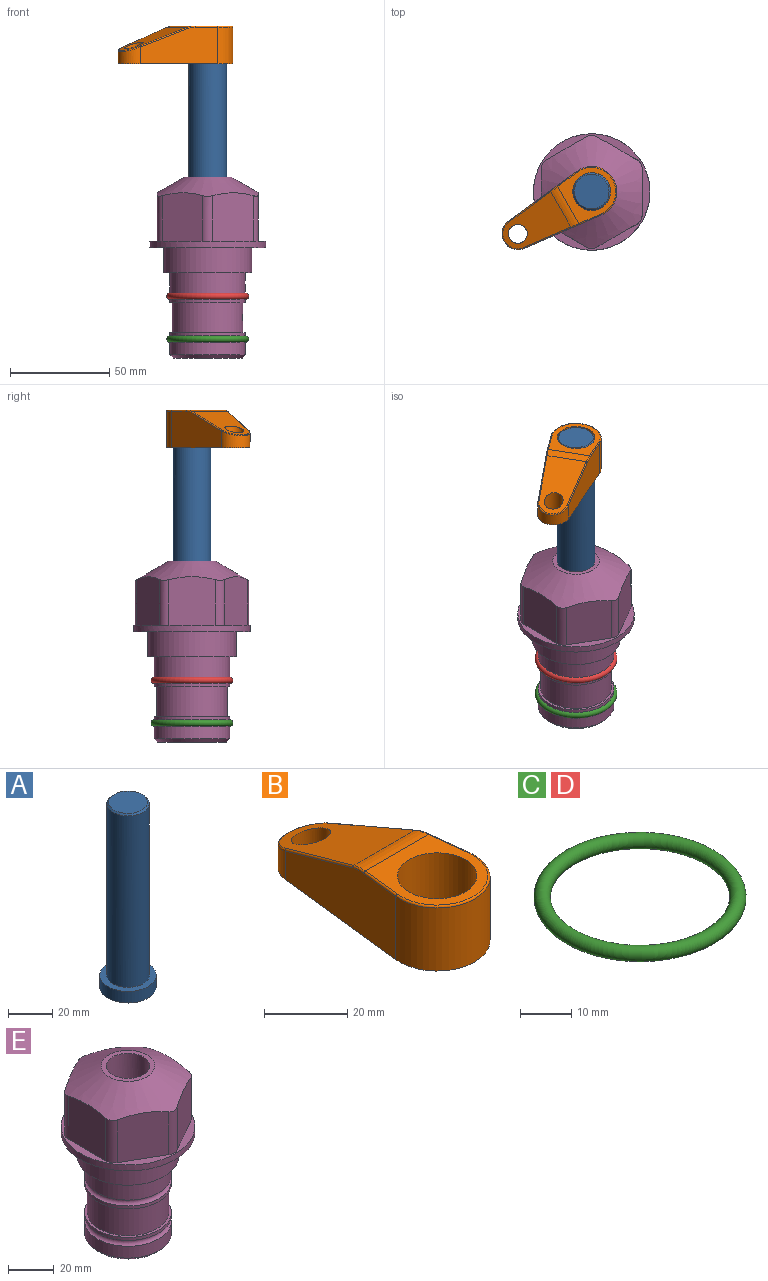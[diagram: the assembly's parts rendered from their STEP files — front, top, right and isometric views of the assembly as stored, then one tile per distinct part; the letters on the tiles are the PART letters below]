
ASSEMBLY  parts=5 mates=3
PART A: 6 faces, bbox 25.4x25.4x101.6 mm
  f0: plane 17.46x17.46mm, normal (0,0,1), area 239.5mm2, adj f5
  f1: plane 25.4x25.4mm, normal (0,0,-1), area 506.7mm2, adj f2
  f2: cylinder r=12.7mm len=25.4mm, axis (0,0,1), area 506.7mm2, adj f1,f3
  f3: plane 25.4x25.4mm, normal (0,0,1), area 221.7mm2, adj f2,f4
  f4: cylinder r=9.53mm len=94.46mm, axis (0,0,1), area 5653mm2, adj f3,f5
  f5: cone r=8.73mm half-angle=45deg, axis (0,0,-1), area 64.4mm2, adj f0,f4
PART B: 44 faces, bbox 27.5x64.5x19.1 mm
  f0: plane 2.3x0.95mm, normal (0,0,-1), area 1mm2, adj f25,f30,f34
  f1: plane 63.5x25.4mm, normal (0,0,-1), area 561.7mm2, adj f2,f3,f4,f5,f6,f7,f19,f20
  f2: cylinder r=12.7mm len=25.4mm, axis (0,0,-1), area 792.2mm2, adj f1,f3,f5,f13
  f3: plane 42.33x18.54mm, normal (0.99,0.11,0), area 647mm2, adj f1,f2,f4,f11,f12,f14
  f4: cylinder r=7.94mm len=15.78mm, axis (0,0,-1), area 158.6mm2, adj f1,f3,f5,f16
  f5: plane 42.33x18.54mm, normal (-0.99,0.11,0), area 647mm2, adj f1,f2,f4,f15,f17,f18
  f6: cylinder r=9.53mm len=19.05mm, axis (0,0,-1), area 1140.1mm2, adj f1,f8
  f7: cylinder r=4.76mm len=10.98mm, axis (0,0,-1), area 276.1mm2, adj f1,f9
  f8: plane 25.83x24.38mm, normal (0,0,1), area 262.2mm2, adj f6,f10,f11,f13,f15
  f9: plane 32.49x20.55mm, normal (0,0.34,0.94), area 489.9mm2, adj f7,f10,f14,f16,f18
  f10: cylinder r=12.7mm len=21.49mm, axis (-1,0,0), area 93.2mm2, adj f8,f9,f12,f17
  f11: cylinder r=0.51mm len=12.34mm, axis (0.11,-0.99,0), area 9.9mm2, adj f3,f8,f12,f13
  f12: bspline ~7.62x1.64mm, area 3.5mm2, adj f3,f10,f11,f14
  f13: torus R=12.19mm, axis (0,0,1), area 33.6mm2, adj f2,f8,f11,f15
  f14: cylinder r=0.51mm len=26.01mm, axis (0.1,-0.93,0.34), area 21.6mm2, adj f3,f9,f12,f16
  f15: cylinder r=0.51mm len=12.34mm, axis (0.11,0.99,0), area 9.9mm2, adj f5,f8,f13,f17
  f16: bspline ~15.78x7.05mm, area 15.7mm2, adj f4,f9,f14,f18
  f17: bspline ~7.62x1.64mm, area 3.5mm2, adj f5,f10,f15,f18
  f18: cylinder r=0.51mm len=26.01mm, axis (0.1,0.93,-0.34), area 21.6mm2, adj f5,f9,f16,f17
  f19: plane 21.6x14.29mm, normal (-0.99,-0.11,0), area 242.6mm2, adj f1,f26,f28,f34,f36,f38
  f20: plane 21.6x14.29mm, normal (0.99,-0.11,0), area 242.6mm2, adj f1,f27,f29,f37,f39,f41
  f21: cylinder r=12.7mm len=14.29mm, axis (0,0,-1), area 173.2mm2, adj f1,f26,f27,f30,f31,f33
  f22: cylinder r=7.94mm len=7.63mm, axis (0,0,-1), area 53.8mm2, adj f1,f28,f29,f42
  f23: plane 2.3x0.95mm, normal (0,0,-1), area 1mm2, adj f25,f33,f37
  f24: plane 17.94x12.32mm, normal (0,-0.34,-0.94), area 191.2mm2, adj f25,f38,f41,f42
  f25: cylinder r=9.53mm len=12.93mm, axis (-1,0,0), area 37.5mm2, adj f0,f23,f24,f31,f36,f39
  f26: cylinder r=1.59mm len=14.29mm, axis (0,0,-1), area 49mm2, adj f1,f19,f21,f32
  f27: cylinder r=1.59mm len=14.29mm, axis (0,0,-1), area 49mm2, adj f1,f20,f21,f35
  f28: cylinder r=1.59mm len=7.28mm, axis (0,0,-1), area 22.1mm2, adj f1,f19,f22,f40
  f29: cylinder r=1.59mm len=7.28mm, axis (0,0,-1), area 22.1mm2, adj f1,f20,f22,f43
  f30: torus R=14.29mm, axis (0,0,1), area 5.8mm2, adj f0,f21,f31,f32
  f31: bspline ~11.06x2.73mm, area 20.8mm2, adj f21,f25,f30,f33
  f32: sphere r=1.59mm, area 5.4mm2, adj f26,f30,f34
  f33: torus R=14.29mm, axis (0,0,1), area 5.8mm2, adj f21,f23,f31,f35
  f34: cylinder r=1.59mm len=1.68mm, axis (-0.11,0.99,0), area 2.4mm2, adj f0,f19,f32,f36
  f35: sphere r=1.59mm, area 5.4mm2, adj f27,f33,f37
  f36: bspline ~5.82x2.33mm, area 7.7mm2, adj f19,f25,f34,f38
  f37: cylinder r=1.59mm len=1.68mm, axis (0.11,0.99,0), area 2.4mm2, adj f20,f23,f35,f39
  f38: cylinder r=1.59mm len=18.33mm, axis (0.1,-0.93,0.34), area 46.7mm2, adj f19,f24,f36,f40
  f39: bspline ~5.82x2.33mm, area 7.7mm2, adj f20,f25,f37,f41
  f40: sphere r=1.59mm, area 3.6mm2, adj f28,f38,f42
  f41: cylinder r=1.59mm len=18.33mm, axis (0.1,0.93,-0.34), area 46.7mm2, adj f20,f24,f39,f43
  f42: bspline ~8.31x1.84mm, area 15.3mm2, adj f22,f24,f40,f43
  f43: sphere r=1.59mm, area 3.6mm2, adj f29,f41,f42
PART C: 1 faces, bbox 44.7x44.7x3.2 mm
  f0: torus R=19.05mm, axis (0,0,1), area 1193.9mm2
PART D: same geometry as C
PART E: 36 faces, bbox 58.7x58.7x91.2 mm
  f0: cylinder r=17.78mm len=35.56mm, axis (0,0,1), area 1670.8mm2, adj f23,f24,f31
  f1: cylinder r=19.05mm len=38.1mm, axis (0,0,1), area 1191.9mm2, adj f26,f27,f30
  f2: plane 58.66x58.66mm, normal (0,0,-1), area 1150.6mm2, adj f3,f28
  f3: cylinder r=29.33mm len=58.66mm, axis (0,0,-1), area 585.1mm2, adj f2,f4
  f4: plane 58.66x58.66mm, normal (0,0,1), area 475.9mm2, adj f3,f5,f6,f7,f8,f9,f10,f11
  f5: plane 24.5x20.32mm, normal (-0.5,0.87,0), area 562.8mm2, adj f4,f15,f16,f17
  f6: plane 24.5x20.32mm, normal (0.5,0.87,0), area 562.8mm2, adj f4,f14,f15,f17
  f7: plane 24.5x23.48mm, normal (1,0,0), area 562.8mm2, adj f4,f13,f14,f17
  f8: plane 24.5x20.32mm, normal (0.5,-0.87,0), area 562.8mm2, adj f4,f12,f13,f17
  f9: plane 24.5x20.32mm, normal (-0.5,-0.87,0), area 562.8mm2, adj f4,f11,f12,f17
  f10: plane 24.5x23.48mm, normal (-1,0,0), area 562.8mm2, adj f4,f11,f16,f17
  f11: cylinder r=5.08mm len=23.01mm, axis (0,0,-1), area 121.2mm2, adj f4,f9,f10,f17
  f12: cylinder r=5.08mm len=23.01mm, axis (0,0,-1), area 121.2mm2, adj f4,f8,f9,f17
  f13: cylinder r=5.08mm len=23.01mm, axis (0,0,-1), area 121.2mm2, adj f4,f7,f8,f17
  f14: cylinder r=5.08mm len=23.01mm, axis (0,0,-1), area 121.2mm2, adj f4,f6,f7,f17
  f15: cylinder r=5.08mm len=23.01mm, axis (0,0,-1), area 121.2mm2, adj f4,f5,f6,f17
  f16: cylinder r=5.08mm len=23.01mm, axis (0,0,-1), area 121.2mm2, adj f4,f5,f10,f17
  f17: cone r=11.73mm half-angle=60deg, axis (0,0,-1), area 2071.8mm2, adj f5,f6,f7,f8,f9,f10,f11,f12
  f18: plane 23.46x23.46mm, normal (0,0,1), area 147.4mm2, adj f17,f35
  f19: plane 34.93x34.93mm, normal (0,0,-1), area 958mm2, adj f29
  f20: cylinder r=19.05mm len=38.1mm, axis (0,0,1), area 760.1mm2, adj f21,f29
  f21: torus R=19.05mm, axis (0,0,1), area 565.3mm2, adj f20,f22
  f22: cylinder r=19.05mm len=38.1mm, axis (0,0,1), area 190mm2, adj f21,f23
  f23: plane 38.1x38.1mm, normal (0,0,1), area 146.9mm2, adj f0,f22
  f24: plane 38.1x38.1mm, normal (0,0,-1), area 146.9mm2, adj f0,f25
  f25: cylinder r=19.05mm len=38.1mm, axis (0,0,1), area 190mm2, adj f24,f26
  f26: torus R=19.05mm, axis (0,0,1), area 565.3mm2, adj f1,f25
  f27: plane 44.45x44.45mm, normal (0,0,-1), area 411.7mm2, adj f1,f28
  f28: cylinder r=22.23mm len=44.45mm, axis (0,0,1), area 1773.5mm2, adj f2,f27
  f29: cone r=19.05mm half-angle=45deg, axis (0,0,1), area 257.5mm2, adj f19,f20
  f30: cylinder r=3.17mm len=6.75mm, axis (-1,0,0), area 128mm2, adj f1,f33
  f31: cylinder r=3.17mm len=6.35mm, axis (-1,0,0), area 102.5mm2, adj f0,f33
  f32: plane 25.4x25.4mm, normal (0,0,1), area 506.7mm2, adj f33
  f33: cylinder r=12.7mm len=66.42mm, axis (0,0,-1), area 5236.2mm2, adj f30,f31,f32,f34
  f34: cone r=9.53mm half-angle=30deg, axis (0,0,-1), area 443.4mm2, adj f33,f35
  f35: cylinder r=9.53mm len=19.05mm, axis (0,0,-1), area 849mm2, adj f18,f34
PLACE A rot(axis=(0,0,-1),150.2deg) t=(0,0,38.01)mm
PLACE B rot(axis=(0,0,1),119.8deg) t=(0,0,92.62)mm
PLACE C t=(0,0,-21.59)mm
PLACE D at identity
PLACE E at identity fixed
MATE fastened C.f0 <-> E.f0  axis (0,0,1) through (0,0,-46.1)mm
MATE cylindrical A.f2 <-> E.f0  axis (0,0,1) through (0,0,63.64)mm
MATE fastened B.f2 <-> A.f2  axis (0,0,1) through (0,0,111.67)mm
